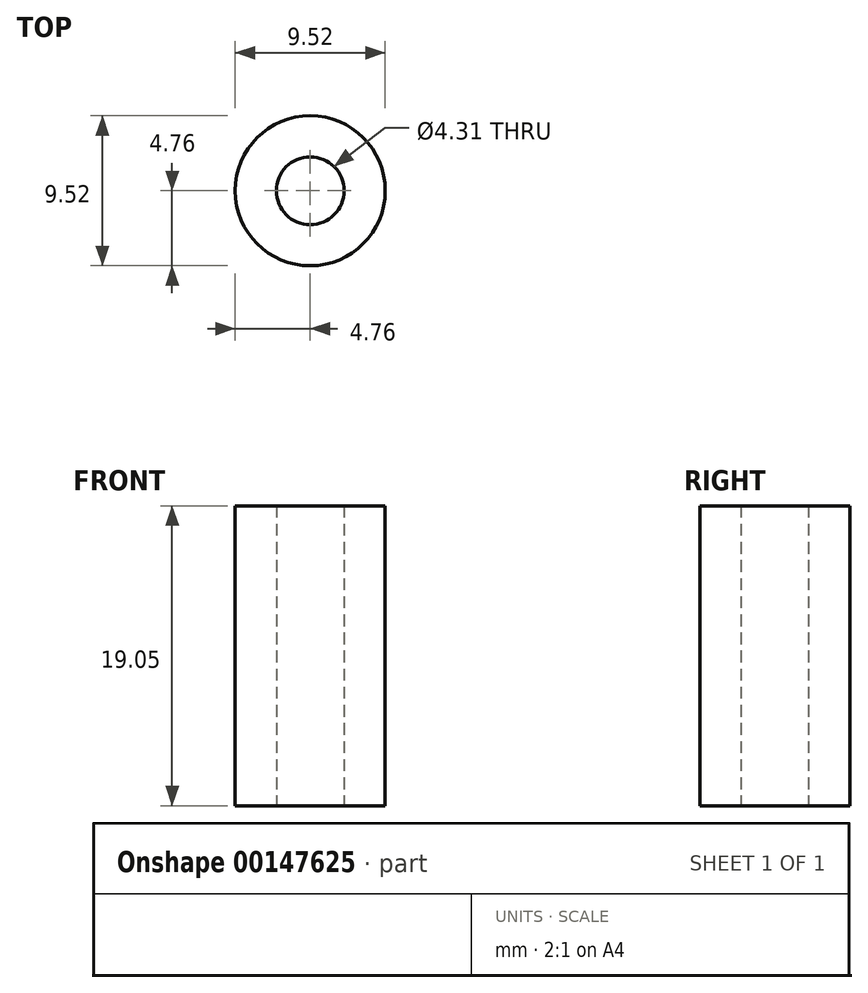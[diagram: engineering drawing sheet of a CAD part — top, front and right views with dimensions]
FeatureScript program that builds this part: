
annotation { "Feature Type Name" : "Feature", "Feature Type Description" : "" }
export const myFeature = defineFeature(function(context is Context, id is Id, definition is map)
    precondition{}
    {
        {
            var Q0;
            Q0=qCreatedBy(makeId("Top.planeOp"),FACE);
            var sketch = newSketch(context, id + "F0", { "sketchPlane" : qUnion([Q0])});
            skCircle(sketch, "E0", {"center": v(0, 0) * mm, "radius": 4.76 * mm});
            skCircle(sketch, "E1", {"center": v(0, 0) * mm, "radius": 2.15 * mm});
            skSolve(sketch);
        }
        {
            var Q0;
            Q0=qSketchRegion(id+"F0",true);
            extrude(context, id + "F1", {"entities" : qUnion([Q0]), "depth" : 19.05 * mm});
        }
    });
